# Revit family: LC6HL
name_source: partatom
category: Lighting Fixtures
revit_build: Autodesk Revit 2014 (Build: 20130308_1515(x64)
units: mm (PartAtom-declared; Revit-internal decimal feet)

## types (3) — shared parameters
Apparent Load = 52 VA
Ceiling Cutout = 6 1/2"
Color Filter = 16777215
Connector Description = Lighting Connector
Cutout Radius = 3"
Default Elevation = 48"
Description = 6 Inch High Lumen LED Downlight
Dimming Lamp Color Temperature Shift = <None>
Emit Shape Visible in Rendering = Yes
Emit from Circle Diameter = 6"
Frequency = 60 Hz
Housing Options = 0-10V dimming to 10%
Input Current = 245 A
Is 120V = Yes
Is 277V = No
Lamp = 6 Inch commercial grade high lumen LED downlight
Load Classification = Lighting
Manufacturer = Prescolite
Manufacturer Fax = 866-898-0131
Model = LC6HL
Product Material = Metal - Hubbell - Stainless Steel
Reflector Finish = Paint - Hubbell - White
Tilt Angle = -90.00°
Trim Aperture = 6 inch Open Reflector/Light EngineAssembly
URL = http://www.prescolite.com
Voltage = 120 V
Wattage Comments = 52-68 W

## per-type parameters (varying)
| type | Photometric Web File |
| 16.00469 | 16.00469.ies |
| 16.00471 | 16.00471.ies |
| 16.00476 | 16.00476.ies |

## geometry (parser evidence)
native form markers: Blend x2, Sweep x3
no freeform markers — native parametric forms only
